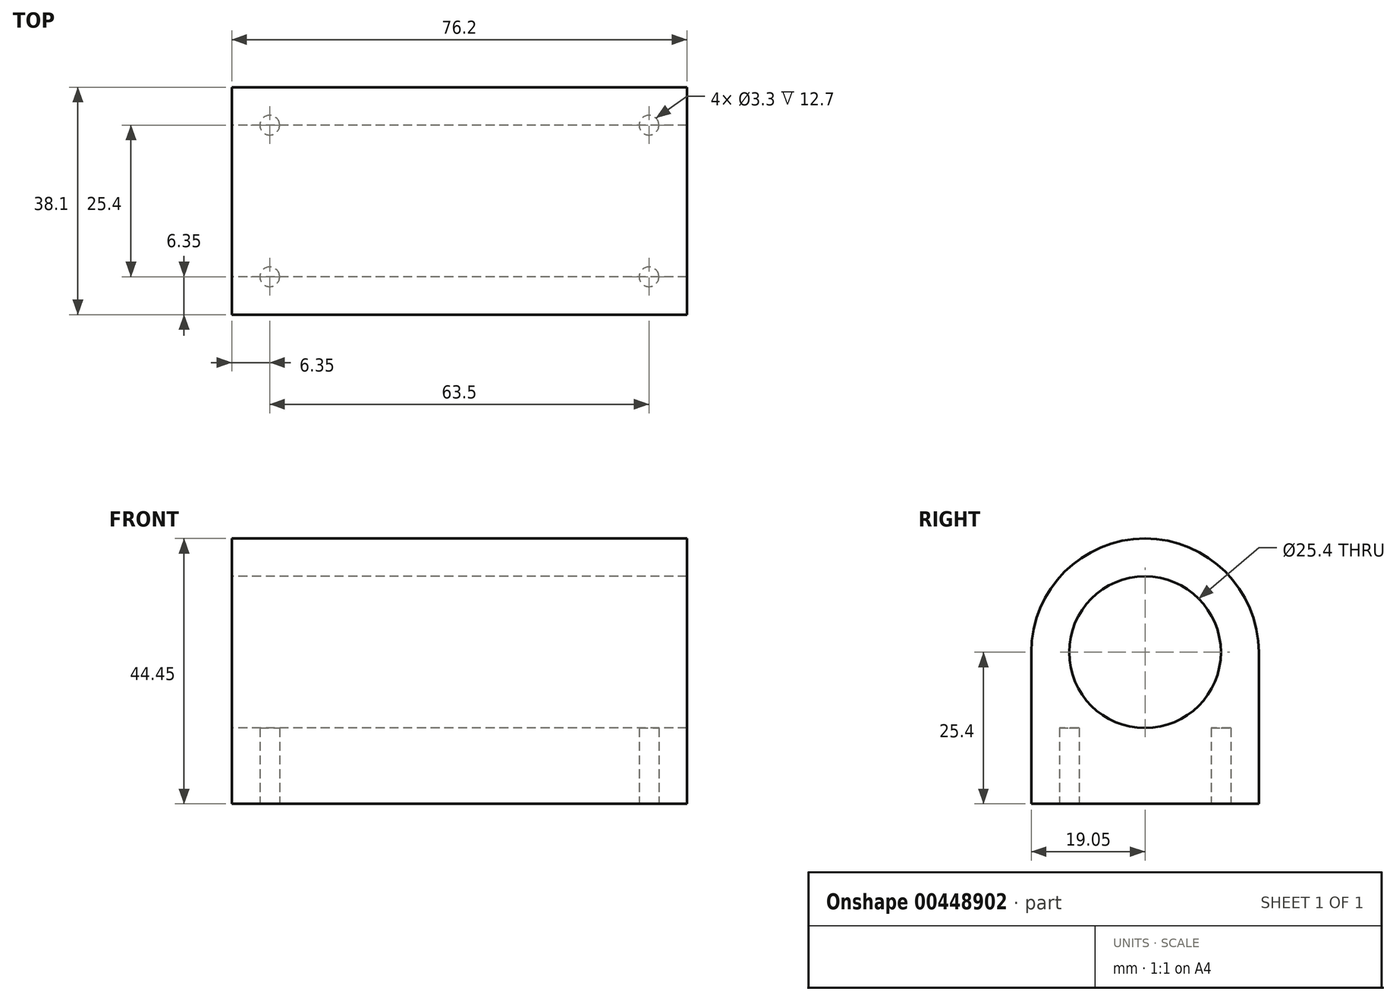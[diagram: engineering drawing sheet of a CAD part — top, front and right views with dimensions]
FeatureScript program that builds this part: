
annotation { "Feature Type Name" : "Feature", "Feature Type Description" : "" }
export const myFeature = defineFeature(function(context is Context, id is Id, definition is map)
    precondition{}
    {
        {
            var Q0;
            Q0=qCreatedBy(makeId("Right.planeOp"),FACE);
            var sketch = newSketch(context, id + "F0", { "sketchPlane" : qUnion([Q0])});
            skCircle(sketch, "E0", {"center": v(0, 0) * mm, "radius": 12.7 * mm});
            skArc(sketch, "E1", {"start": v(19.05, 0) * mm, "mid": v(0, 19.05) * mm, "end": v(-19.05, 0) * mm});
            skLineSegment(sketch, "E2", {"start": v(-19.05, 0) * mm, "end": v(-19.05, -25.4) * mm});
            skLineSegment(sketch, "E3", {"start": v(-19.05, -25.4) * mm, "end": v(19.05, -25.4) * mm});
            skLineSegment(sketch, "E4", {"start": v(19.05, -25.4) * mm, "end": v(19.05, 0) * mm});
            skSolve(sketch);
        }
        {
            var Q0;
            Q0 = qSketchRegion(id + "F0", true);
            extrude(context, id + "F1", {"entities" : qUnion([Q0]), "endBound" : BoundingType.SYMMETRIC, "depth" : 76.2 * mm});
        }
        {
            var Q0;
            Q0=makeQuery(id+"F1.opExtrude","SWEPT_FACE",FACE,{"disambiguationData":[OSD([sQuery(id+"F0.wireOp",EDGE,"E3")])]});
            var sketch = newSketch(context, id + "F2", { "sketchPlane" : qUnion([Q0])});
            skCircle(sketch, "E5", {"center": v(-31.75, 12.7) * mm, "radius": 1.65 * mm});
            skCircle(sketch, "E6", {"center": v(-31.75, -12.7) * mm, "radius": 1.65 * mm});
            skCircle(sketch, "E7", {"center": v(31.75, -12.7) * mm, "radius": 1.65 * mm});
            skCircle(sketch, "E8", {"center": v(31.75, 12.7) * mm, "radius": 1.65 * mm});
            skSolve(sketch);
        }
        {
            var Q0;
            Q0 = qSketchRegion(id + "F2", true);
            extrude(context, id + "F3", {"entities" : qUnion([Q0]), "operationType" : NewBodyOperationType.REMOVE, "oppositeDirection" : true, "depth" : 12.7 * mm});
        }
    });
